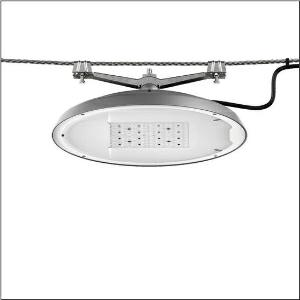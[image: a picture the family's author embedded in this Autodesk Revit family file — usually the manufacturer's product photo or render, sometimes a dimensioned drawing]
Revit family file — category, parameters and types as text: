
# Revit family: dl_r__50_iq_mini___st0_8s_5xa248v31f08le_222e
name_source: partatom
category: Lighting Fixtures
units: mm (PartAtom-declared; Revit-internal decimal feet)

## family parameters
Cut with Voids When Loaded = No
Host = Face
Light Source = No
Part Type = Normal
Room Calculation Point = No
Round Connector Dimension = Use Diameter
Shared = No

## types (1)
- --- (1 x LED, 10390 lm, 67.4 W, 3000K)
    Apparent Load = 67 VA
    CIE Flux Codes = 38 75 97 100 100
    Color Rendering = 70
    Color Temperature = 3000K
    Default Elevation = 1800 mm
    Description = DL® 50 iQ mini, catenary luminaire, primary light control with lens, of PMMA, primary optical cover: cover, of toughened safety glass, transparent, light distribution: ST0.8s, light emission: direct distribution, primary light characteristic: symmetric, installation type: suspended mounting, LED, High Power LED, rated luminous flux: 10.390lm, luminous efficacy: 154lm/W, light colour: 730, colour temperature: 3000K, control: optimised constant luminous flux control (CLO 2.0), Desk-Remote (wireless, voltage-free reading and setting of iQ features in the workshop via application-optimized NFC function/RFID function), Light-Fading, Smart-Wire, Night-Set, Lumen-Switch, Temp-Guard, Auto-Match, Street-Remote, mains connection: 230..240V, AC, 50/60Hz, start of lifetime: 67W, end of service life: 70W, reduction: 31W, luminaire housing, of diecast aluminium, powder-coated, Siteco® metallic grey (DB 702S), diameter: 500mm, height: 115mm, protection rating (complete): IP66, insulation class (complete): insulation class II (safety insulation), certification: CE, ENEC, VDE, impact resistance: IK08, permissible operating ambient temperature for outdoor applications: -25..+40°C, standard-compliant lighting for roads and squares, packaging unit: 1 piece

Light Distribution: ST0.8s
    Height = 124 mm  [stored 0.406824 ft]
    Lamp = 1 x LED
    Lamp Light Flux = 10390 lm
    Lamp Power = 67.4 W
    Lamp count = 1
    Length = 500 mm
    Luminous efficacy = 154 lm/W
    Manufacturer = Siteco
    ModVariant = No
    Model = 5XA248V31F08LE
    Number of Poles = 1
    OnlyDefault = Yes
    Power Factor = 1
    Product Name = DL® 50 iQ mini | ST0.8s
    Product group = catenary luminaire
    ProductGroupID = 6300
    Protection Class = Protection class II
    Protection Degree = IP 66
    RLX_Detail_Level = 1
    RLX_Emergency_Light_Flux = 0 lm
    RLX_Emergency_Type = 0
    RLX_Emergency_Type_DB = No
    RlxData = <blob elided: 126945 chars, md5=23030bc5>
    Socket = socket
    Standby Power = 0 W
    System Light Flux = 10390 lm
    System Power = 67 W
    Type Comments = factory setting: luminous flux: 100 % | dim-lin: 254 | 705 mA
    Type Image = l_1251783.jpg
    URL = http://relux.com
    VarID = @adj_090427
    Voltage = 0 V
    Weight = 0.00 kg
    Width = 0 mm  [stored 0 ft]

note: [stored X ft] marks values corroborated as IEEE doubles in the binary element streams (Revit-internal decimal feet)

## geometry (parser evidence)
native form markers: Blend x4, Sweep x13
no freeform markers — native parametric forms only
